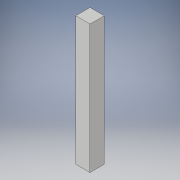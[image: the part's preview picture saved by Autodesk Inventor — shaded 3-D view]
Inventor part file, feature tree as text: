
AUTODESK INVENTOR PART (.ipt)
format: ipt  version: 2017 (Build 210142000, 142)  size: 91,136 bytes
history: native  units: in
note: dims shown in document units (in); Inventor stores cm internally (conversion verified against a paired STEP export)
features: extrude x1, sketch x1
ambient origin geometry x8: Origin, YZ Plane, XZ Plane, XY Plane, X Axis, Y Axis, Z Axis, Center Point
bodies: Solid1 (feature_tree)
feature tree (2):
  extrude  "Extrusion1"  Depth=18.0in
  sketch  "Sketch1"  dims[d0=2.0in d1=18.0in d2=2.0in d3=0.0in]
